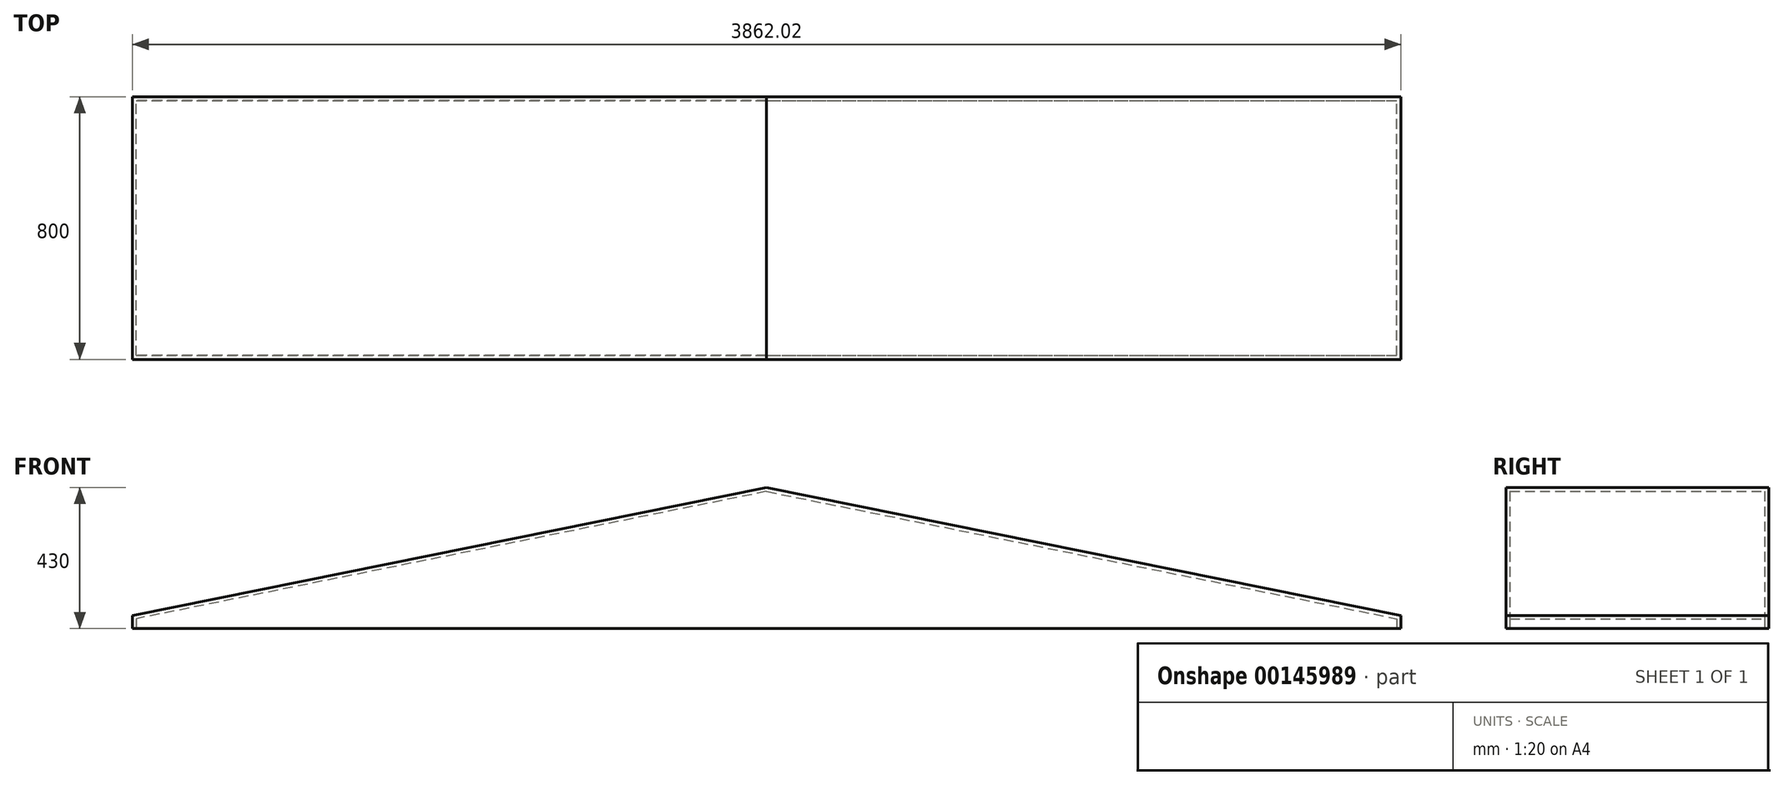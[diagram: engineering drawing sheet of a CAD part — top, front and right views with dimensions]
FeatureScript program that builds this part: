
annotation { "Feature Type Name" : "Feature", "Feature Type Description" : "" }
export const myFeature = defineFeature(function(context is Context, id is Id, definition is map)
    precondition{}
    {
        {
            var Q0;
            Q0=qCreatedBy(makeId("Front.planeOp"),FACE);
            var sketch = newSketch(context, id + "F0", { "sketchPlane" : qUnion([Q0])});
            skLineSegment(sketch, "E0", {"start": v(63.84, -12.05) * mm, "end": v(1994.85, -402.05) * mm});
            skLineSegment(sketch, "E1", {"start": v(-1867.17, -402.05) * mm, "end": v(-1867.17, -442.05) * mm});
            skLineSegment(sketch, "E2", {"start": v(-1867.17, -442.05) * mm, "end": v(1994.85, -442.05) * mm});
            skLineSegment(sketch, "E3", {"start": v(1994.85, -402.05) * mm, "end": v(1994.85, -442.05) * mm});
            skLineSegment(sketch, "E4", {"start": v(63.84, -12.05) * mm, "end": v(-1867.17, -402.05) * mm});
            skLineSegment(sketch, "E5", {"start": v(63.84, -12.05) * mm, "end": v(63.84, -442.05) * mm});
            skSolve(sketch);
        }
        {
            var Q0;
            {var subQ0=sQuery(id+"F0.wireOp",EDGE,"E1");Q0=makeQuery(id+"F0.imprint","IMPRINT",FACE,{"disambiguationData":[TD([[makeQuery(id+"F0.imprint","IMPRINT",EDGE,{"derivedFrom":subQ0}),1.0]])]});}
            var Q1;
            Q1=makeQuery(id+"F0.imprint","IMPRINT",FACE,{"disambiguationData":[TD([[makeQuery(id+"F0.imprint","IMPRINT",EDGE,{"derivedFrom":sQuery(id+"F0.wireOp",EDGE,"E0")}),-1.0]])]});
            extrude(context, id + "F1", {"entities" : qUnion([Q0, Q1]), "depth" : 800 * mm});
        }
        {
            var Q0;
            Q0=makeQuery(id+"F1.opExtrude","SWEPT_FACE",FACE,{"disambiguationData":[OSD([sQuery(id+"F0.wireOp",EDGE,"E2")])]});
            shell(context, id + "F2", {"entities" : qUnion([Q0]), "thickness" : 12 * mm});
        }
    });
